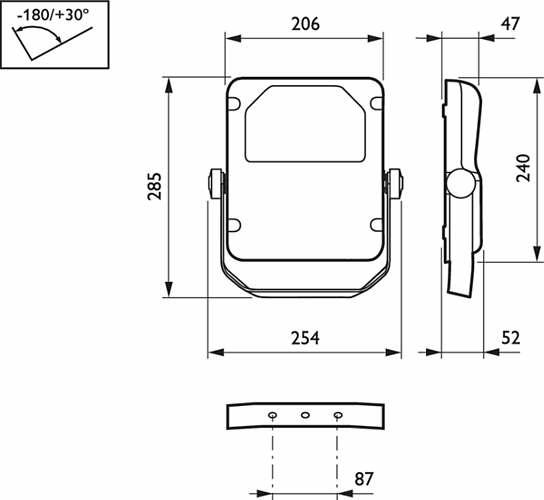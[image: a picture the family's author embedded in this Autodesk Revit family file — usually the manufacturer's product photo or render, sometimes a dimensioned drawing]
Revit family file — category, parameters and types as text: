
# Revit family: 63_PHILIPS_Coreline_tempo_large-BVP130
name_source: partatom
category: Lighting Fixtures
revit_build: Autodesk Revit 2016 (Build: 20150220_1215(x64)
units: mm (PartAtom-declared; Revit-internal decimal feet)

## family parameters
Cut with Voids When Loaded = No
Host = Face
Light Source = No
Part Type = Normal
Room Calculation Point = No
Round Connector Dimension = Use Diameter
Shared = Yes

## types (1)
- 63_PHILIPS_Coreline_tempo_large-BVP130
    Apparent Load = 0 VA
    Default Elevation = 0 mm  [stored 0 ft]
    Description = Coreline tempo large
    Lamp = LAMP TYPE
    Lamp type = BVP130 IES Data : 1 xLED160-4S_740 A
    Manufacturer = Philips
    Model = BVP130
    Type Comments = Face Based
    URL = http://www.lighting.philips.com
    Width = 389 mm  [stored 1.27625 ft]

note: [stored X ft] marks values corroborated as IEEE doubles in the binary element streams (Revit-internal decimal feet)

## geometry (parser evidence)
native form markers: Sweep x11
no freeform markers — native parametric forms only
